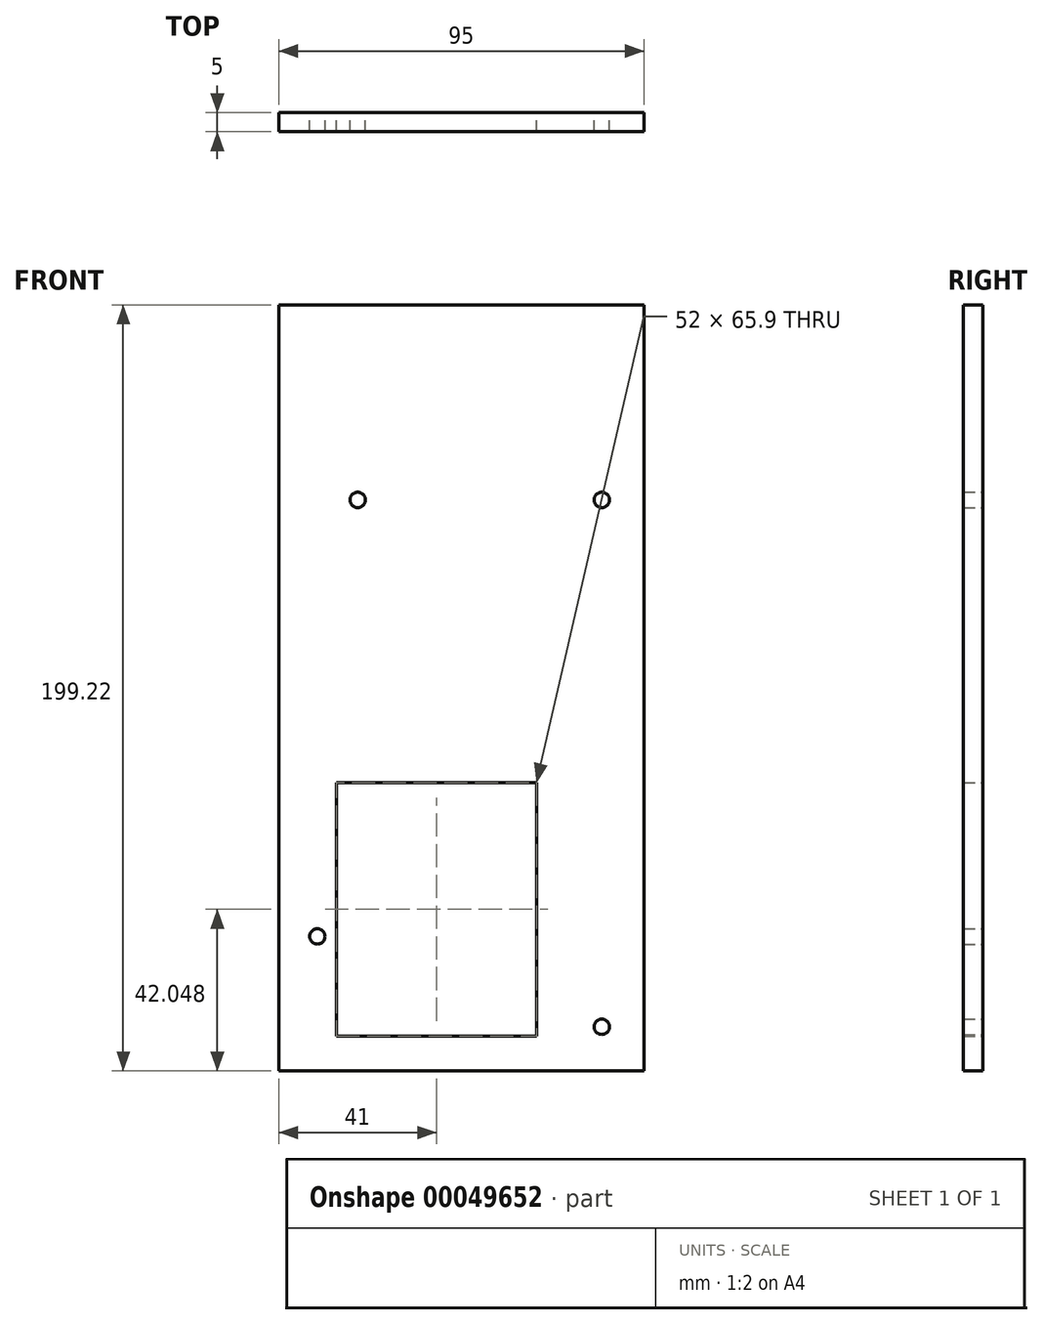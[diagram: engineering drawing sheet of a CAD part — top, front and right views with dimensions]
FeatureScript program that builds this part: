
annotation { "Feature Type Name" : "Feature", "Feature Type Description" : "" }
export const myFeature = defineFeature(function(context is Context, id is Id, definition is map)
    precondition{}
    {
        {
            var Q0;
            Q0=qCreatedBy(makeId("Front.planeOp"),FACE);
            var sketch = newSketch(context, id + "F0", { "sketchPlane" : qUnion([Q0])});
            skLineSegment(sketch, "E0.bottom", {"start": v(0, 0) * mm, "end": v(85, 0) * mm, "construction": true});
            skLineSegment(sketch, "E0.top", {"start": v(0, 150) * mm, "end": v(85, 150) * mm, "construction": true});
            skLineSegment(sketch, "E0.left", {"start": v(0, 0) * mm, "end": v(0, 150) * mm, "construction": true});
            skLineSegment(sketch, "E0.right", {"start": v(85, 0) * mm, "end": v(85, 150) * mm, "construction": true});
            skCircle(sketch, "E1", {"center": v(5, 30) * mm, "radius": 2 * mm});
            skCircle(sketch, "E2", {"center": v(15.5, 143.5) * mm, "radius": 2 * mm});
            skCircle(sketch, "E3", {"center": v(79, 143.5) * mm, "radius": 2 * mm});
            skCircle(sketch, "E4", {"center": v(79, 6.5) * mm, "radius": 2 * mm});
            skLineSegment(sketch, "E5.bottom", {"start": v(-5, -5) * mm, "end": v(90, -5) * mm});
            skLineSegment(sketch, "E5.top", {"start": v(-5, 194.22) * mm, "end": v(90, 194.22) * mm});
            skLineSegment(sketch, "E5.left", {"start": v(-5, -5) * mm, "end": v(-5, 194.22) * mm});
            skLineSegment(sketch, "E5.right", {"start": v(90, -5) * mm, "end": v(90, 194.22) * mm});
            skLineSegment(sketch, "E6.bottom", {"start": v(10, 70) * mm, "end": v(62, 70) * mm});
            skLineSegment(sketch, "E6.top", {"start": v(10, 4.1) * mm, "end": v(62, 4.1) * mm});
            skLineSegment(sketch, "E6.left", {"start": v(10, 70) * mm, "end": v(10, 4.1) * mm});
            skLineSegment(sketch, "E6.right", {"start": v(62, 70) * mm, "end": v(62, 4.1) * mm});
            skSolve(sketch);
        }
        {
            var Q0;
            Q0=makeQuery(id+"F0.imprint","IMPRINT",FACE,{"disambiguationData":[TD([[makeQuery(id+"F0.imprint","IMPRINT",EDGE,{"derivedFrom":sQuery(id+"F0.wireOp",EDGE,"E1")}),-1.0]])]});
            extrude(context, id + "F1", {"entities" : qUnion([Q0]), "depth" : 5 * mm});
        }
    });
